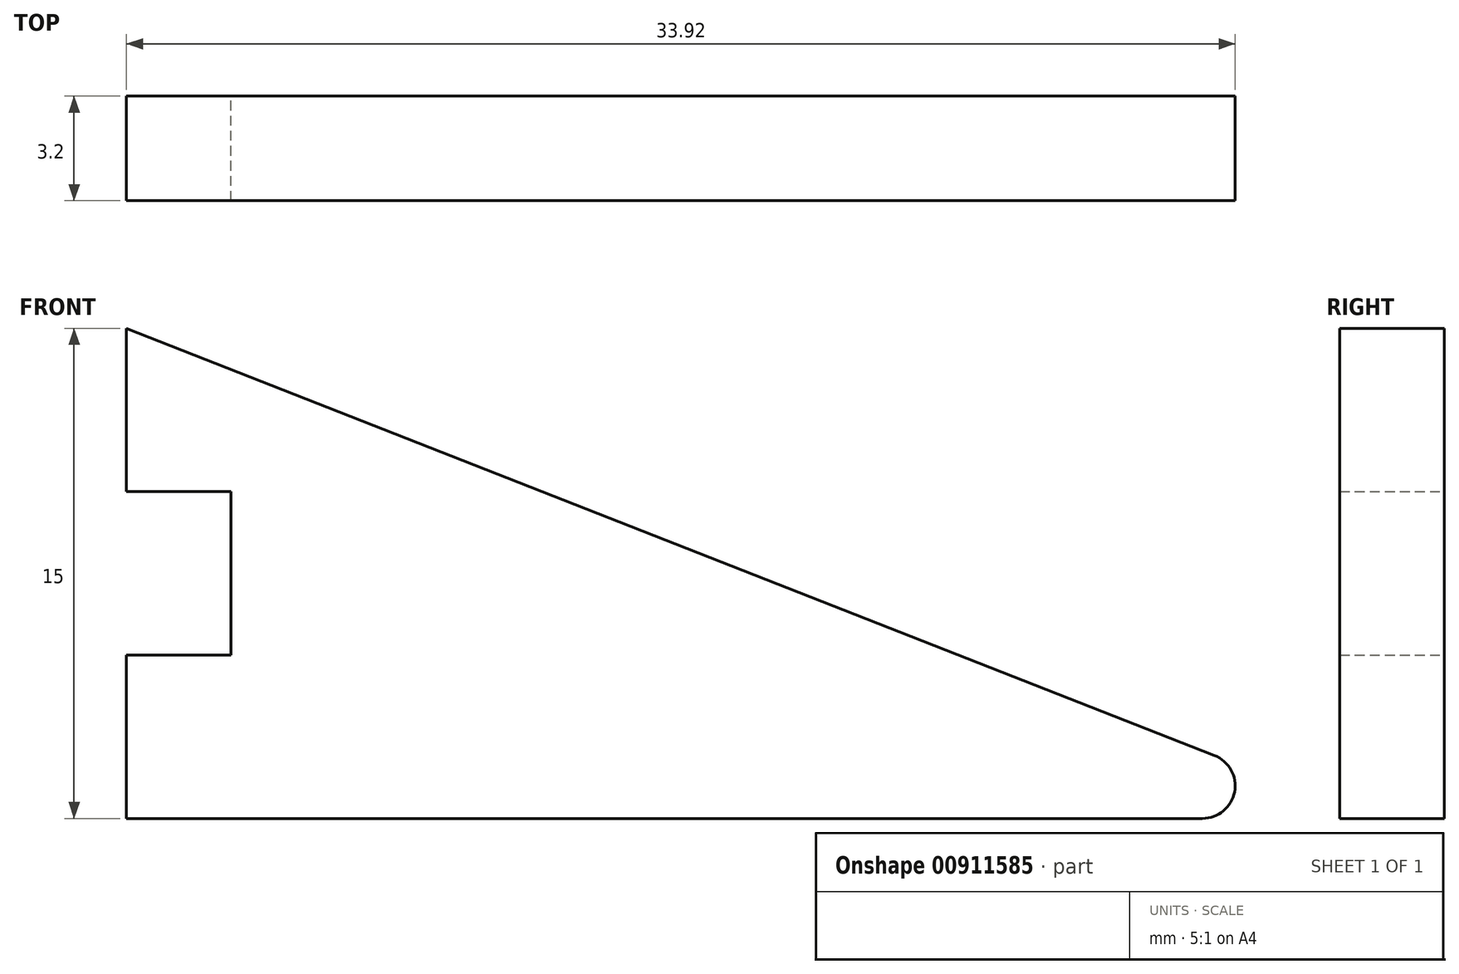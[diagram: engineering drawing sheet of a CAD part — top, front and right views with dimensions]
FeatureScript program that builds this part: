
annotation { "Feature Type Name" : "Feature", "Feature Type Description" : "" }
export const myFeature = defineFeature(function(context is Context, id is Id, definition is map)
    precondition{}
    {
        {
            var Q0;
            Q0=qCreatedBy(makeId("Front.planeOp"),FACE);
            var sketch = newSketch(context, id + "F0", { "sketchPlane" : qUnion([Q0])});
            skLineSegment(sketch, "E0", {"start": v(0, 0) * mm, "end": v(-3.2, 0) * mm});
            skLineSegment(sketch, "E1", {"start": v(-3.2, 0) * mm, "end": v(-3.2, -5) * mm});
            skLineSegment(sketch, "E2", {"start": v(-3.2, -5) * mm, "end": v(0, -5) * mm});
            skLineSegment(sketch, "E3", {"start": v(0, -5) * mm, "end": v(0, -10) * mm});
            skLineSegment(sketch, "E4", {"start": v(0, -10) * mm, "end": v(-3.2, -10) * mm});
            skLineSegment(sketch, "E5", {"start": v(-3.2, -10) * mm, "end": v(-3.2, -15) * mm});
            skLineSegment(sketch, "E6", {"start": v(-3.2, -15) * mm, "end": v(0, -15) * mm});
            skLineSegment(sketch, "E7", {"start": v(0, -15) * mm, "end": v(35, -15) * mm});
            skLineSegment(sketch, "E8", {"start": v(35, -15) * mm, "end": v(-3.2, 0) * mm});
            skSolve(sketch);
        }
        {
            var Q0;
            Q0 = qSketchRegion(id + "F0", true);
            extrude(context, id + "F1", {"entities" : qUnion([Q0]), "depth" : 3.2 * mm, "offsetDistance" : 25 * mm});
        }
        {
            var Q0;
            Q0=makeQuery(id+"F1.opExtrude","SWEPT_EDGE",EDGE,{"disambiguationData":[OSD([sQuery(id+"F0.wireOp",EDGE,"E7"),sQuery(id+"F0.wireOp",EDGE,"E8")])]});
            fillet(context, id + "F2", {"entities" : qUnion([Q0]), "radius" : 1 * mm, "tangentPropagation" : true, "allowEdgeOverflow" : false});
        }
    });
